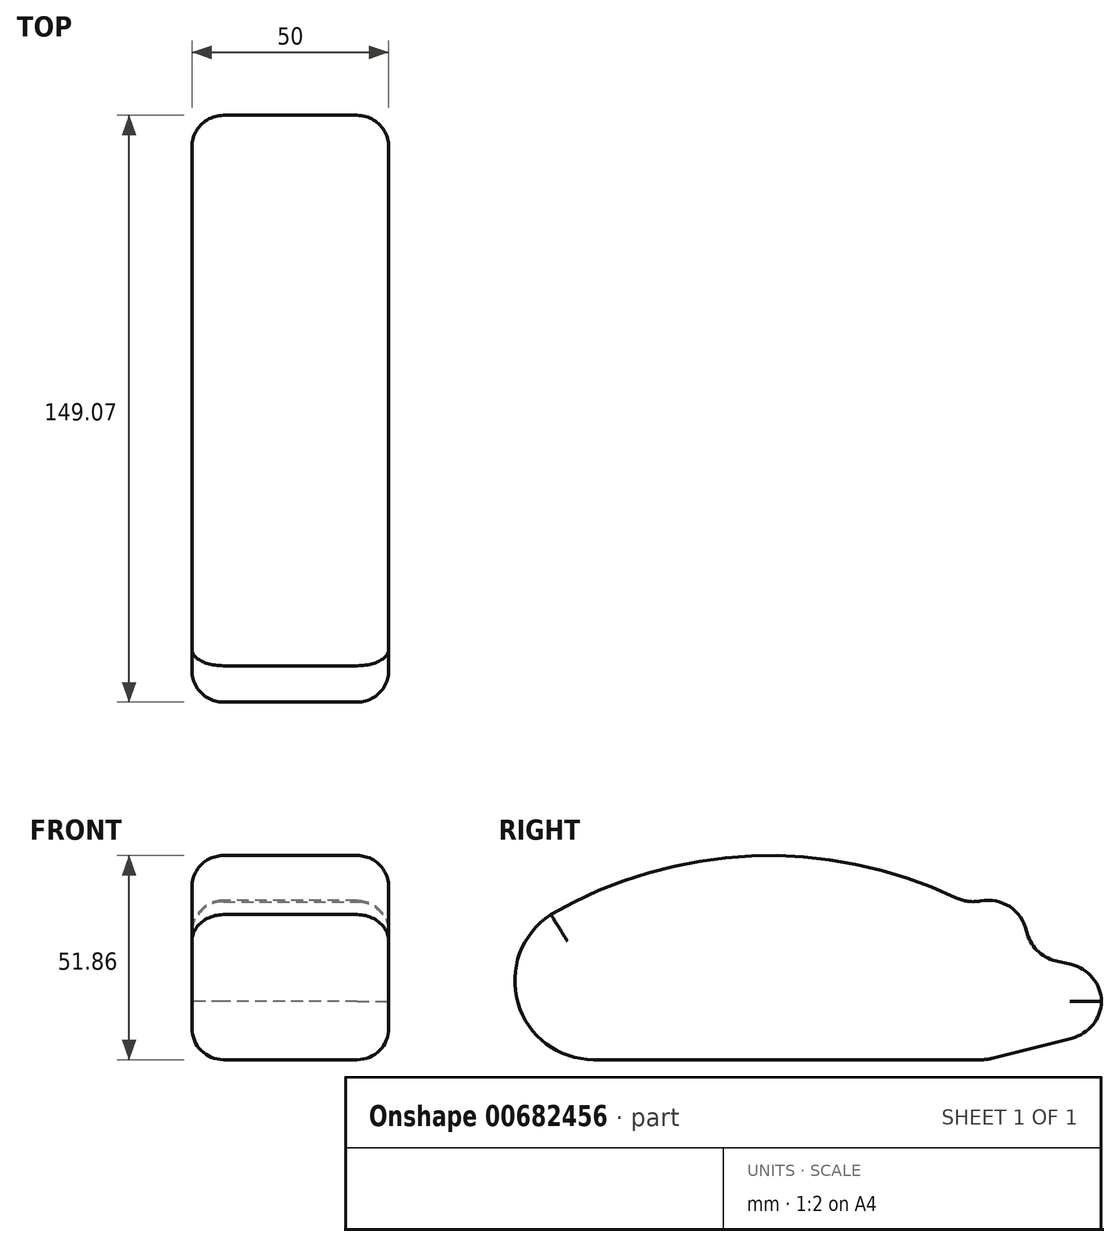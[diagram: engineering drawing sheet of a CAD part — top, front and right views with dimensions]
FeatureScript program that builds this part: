
annotation { "Feature Type Name" : "Feature", "Feature Type Description" : "" }
export const myFeature = defineFeature(function(context is Context, id is Id, definition is map)
    precondition{}
    {
        {
            var Q0;
            Q0=qCreatedBy(makeId("Right.planeOp"),FACE);
            var sketch = newSketch(context, id + "F0", { "sketchPlane" : qUnion([Q0])});
            skLineSegment(sketch, "E0", {"start": v(0, 0) * mm, "end": v(100, 0) * mm});
            skArc(sketch, "E1", {"start": v(-10.78, 36.85) * mm, "mid": v(-19.2, 14.38) * mm, "end": v(0, 0) * mm});
            skArc(sketch, "E2", {"start": v(95.62, 39.37) * mm, "mid": v(42.1, 51.83) * mm, "end": v(-10.78, 36.85) * mm});
            skLineSegment(sketch, "E3", {"start": v(100, 0) * mm, "end": v(129.08, 7.37) * mm});
            skLineSegment(sketch, "E4", {"start": v(129.08, 7.37) * mm, "end": v(129.08, 22.37) * mm});
            skLineSegment(sketch, "E5", {"start": v(129.08, 22.37) * mm, "end": v(109.61, 26.95) * mm});
            skArc(sketch, "E6", {"start": v(109.61, 26.95) * mm, "mid": v(106.9, 38) * mm, "end": v(95.62, 39.37) * mm});
            skSolve(sketch);
        }
        {
            var Q0;
            Q0=makeQuery(id+"F0.imprint","IMPRINT",FACE,{"disambiguationData":[TD([[makeQuery(id+"F0.imprint","IMPRINT",EDGE,{"derivedFrom":sQuery(id+"F0.wireOp",EDGE,"E0")}),1.0]])]});
            extrude(context, id + "F1", {"entities" : qUnion([Q0]), "depth" : 50 * mm, "offsetDistance" : 25 * mm});
        }
        {
            var Q0;
            Q0=makeQuery(id+"F1.opExtrude","SWEPT_EDGE",EDGE,{"disambiguationData":[OSD([sQuery(id+"F0.wireOp",EDGE,"E5"),sQuery(id+"F0.wireOp",EDGE,"E6")])]});
            var Q1;
            Q1=makeQuery(id+"F1.opExtrude","SWEPT_EDGE",EDGE,{"disambiguationData":[OSD([sQuery(id+"F0.wireOp",EDGE,"E2"),sQuery(id+"F0.wireOp",EDGE,"E6")])]});
            var Q2;
            Q2=makeQuery(id+"F1.opExtrude","SWEPT_EDGE",EDGE,{"disambiguationData":[OSD([sQuery(id+"F0.wireOp",EDGE,"E4"),sQuery(id+"F0.wireOp",EDGE,"E5")])]});
            var Q3;
            Q3=makeQuery(id+"F1.opExtrude","SWEPT_EDGE",EDGE,{"disambiguationData":[OSD([sQuery(id+"F0.wireOp",EDGE,"E3"),sQuery(id+"F0.wireOp",EDGE,"E4")])]});
            var Q4;
            Q4=makeQuery(id+"F1.opExtrude","SWEPT_EDGE",EDGE,{"disambiguationData":[OSD([sQuery(id+"F0.wireOp",EDGE,"E0"),sQuery(id+"F0.wireOp",EDGE,"E3")])]});
            fillet(context, id + "F2", {"entities" : qUnion([Q0, Q1, Q2, Q3, Q4]), "radius" : 10 * mm, "tangentPropagation" : true, "allowEdgeOverflow" : false});
        }
        {
            var Q0;
            Q0=makeQuery(id+"F1.opExtrude","CAP_EDGE",EDGE,{"disambiguationData":[OSD([sQuery(id+"F0.wireOp",EDGE,"E2")])],"isStart":false});
            var Q1;
            Q1=makeQuery(id+"F1.opExtrude","CAP_EDGE",EDGE,{"disambiguationData":[OSD([sQuery(id+"F0.wireOp",EDGE,"E2")])],"isStart":true});
            var Q2;
            Q2=makeQuery(id+"F1.opExtrude","CAP_FACE",FACE,{"disambiguationData":[OSD([sQuery(id+"F0.wireOp",EDGE,"E0"),sQuery(id+"F0.wireOp",EDGE,"E1"),sQuery(id+"F0.wireOp",EDGE,"E2"),sQuery(id+"F0.wireOp",EDGE,"E3"),sQuery(id+"F0.wireOp",EDGE,"E4"),sQuery(id+"F0.wireOp",EDGE,"E5"),sQuery(id+"F0.wireOp",EDGE,"E6")])],"isStart":false});
            var Q3;
            Q3=makeQuery(id+"F1.opExtrude","CAP_FACE",FACE,{"disambiguationData":[OSD([sQuery(id+"F0.wireOp",EDGE,"E0"),sQuery(id+"F0.wireOp",EDGE,"E1"),sQuery(id+"F0.wireOp",EDGE,"E2"),sQuery(id+"F0.wireOp",EDGE,"E3"),sQuery(id+"F0.wireOp",EDGE,"E4"),sQuery(id+"F0.wireOp",EDGE,"E5"),sQuery(id+"F0.wireOp",EDGE,"E6")])],"isStart":true});
            fillet(context, id + "F3", {"entities" : qUnion([Q0, Q1, Q2, Q3]), "radius" : 8 * mm, "tangentPropagation" : true, "allowEdgeOverflow" : false});
        }
    });
